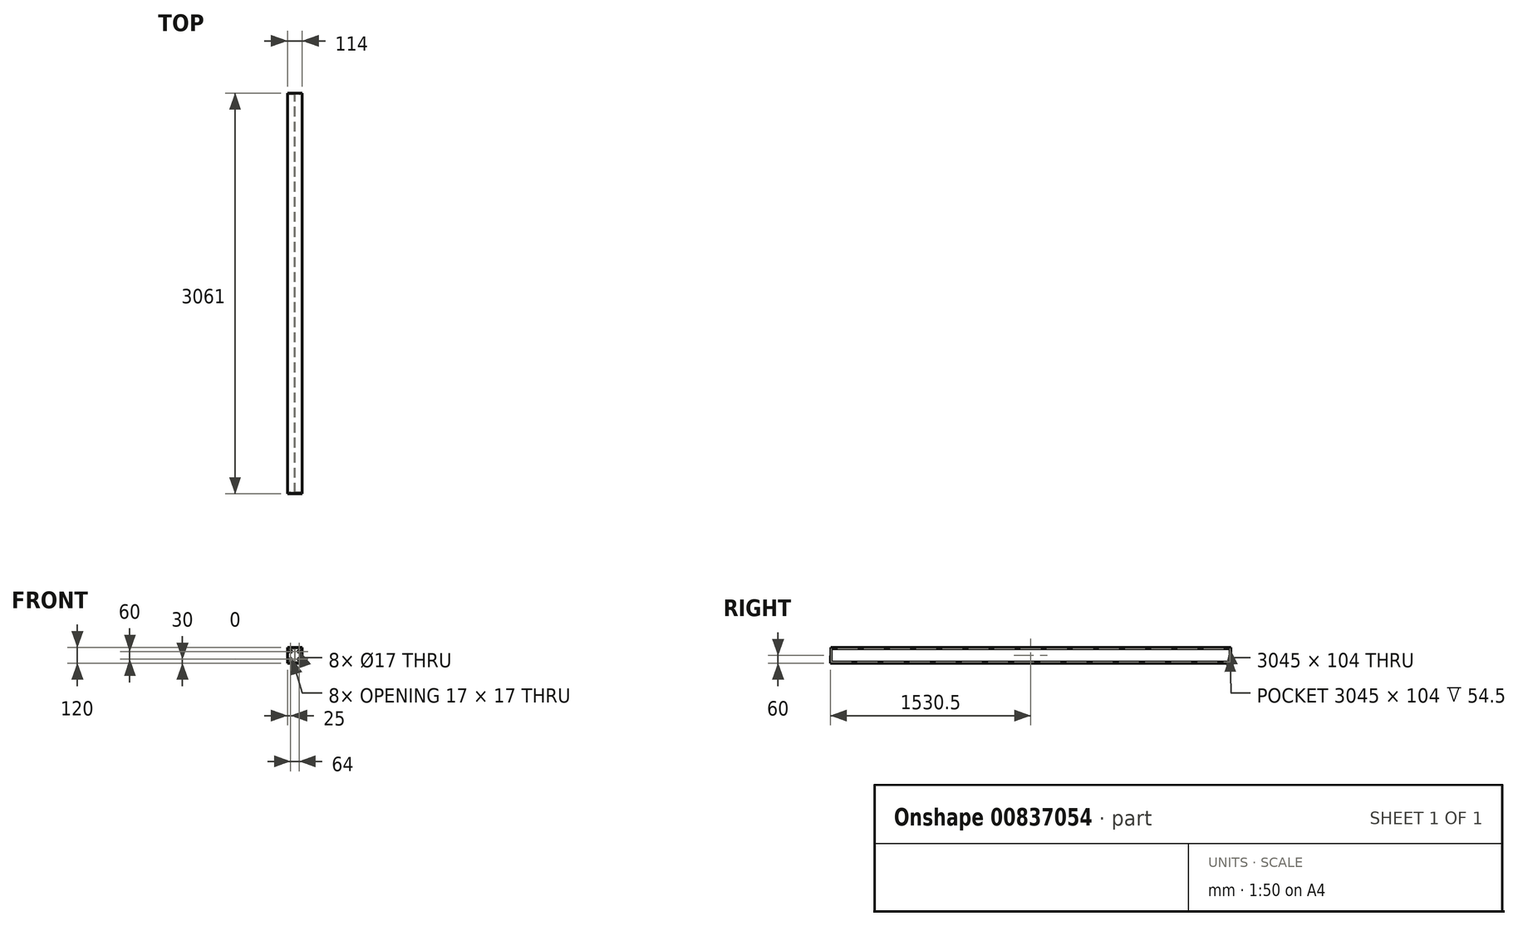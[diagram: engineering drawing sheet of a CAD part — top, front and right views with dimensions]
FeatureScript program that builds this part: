
annotation { "Feature Type Name" : "Feature", "Feature Type Description" : "" }
export const myFeature = defineFeature(function(context is Context, id is Id, definition is map)
    precondition{}
    {
        {
            var Q0;
            Q0=qCreatedBy(makeId("Front.planeOp"),FACE);
            var sketch = newSketch(context, id + "F0", { "sketchPlane" : qUnion([Q0])});
            skLineSegment(sketch, "E0", {"start": v(0, 60) * mm, "end": v(-57, 60) * mm});
            skLineSegment(sketch, "E1", {"start": v(-57, 60) * mm, "end": v(-57, 52) * mm});
            skLineSegment(sketch, "E2", {"start": v(-57, 52) * mm, "end": v(-2.5, 52) * mm});
            skLineSegment(sketch, "E3", {"start": v(-2.5, 52) * mm, "end": v(-2.5, 0) * mm});
            skLineSegment(sketch, "E4.MirrorCS", {"start": v(2.5, 52) * mm, "end": v(2.5, 0) * mm});
            skLineSegment(sketch, "E5.MirrorCS", {"start": v(57, 52) * mm, "end": v(2.5, 52) * mm});
            skLineSegment(sketch, "E6.MirrorCS", {"start": v(0, 60) * mm, "end": v(57, 60) * mm});
            skLineSegment(sketch, "E7.MirrorCS", {"start": v(57, 60) * mm, "end": v(57, 52) * mm});
            skLineSegment(sketch, "E8.MirrorCS", {"start": v(-2.5, -52) * mm, "end": v(-2.5, 0) * mm});
            skLineSegment(sketch, "E9.MirrorCS", {"start": v(-57, -52) * mm, "end": v(-2.5, -52) * mm});
            skLineSegment(sketch, "E10.MirrorCS", {"start": v(-57, -60) * mm, "end": v(-57, -52) * mm});
            skLineSegment(sketch, "E11.MirrorCS", {"start": v(0, -60) * mm, "end": v(-57, -60) * mm});
            skLineSegment(sketch, "E12.MirrorCS", {"start": v(0, -60) * mm, "end": v(57, -60) * mm});
            skLineSegment(sketch, "E13.MirrorCS", {"start": v(57, -60) * mm, "end": v(57, -52) * mm});
            skLineSegment(sketch, "E14.MirrorCS", {"start": v(57, -52) * mm, "end": v(2.5, -52) * mm});
            skLineSegment(sketch, "E15.MirrorCS", {"start": v(2.5, -52) * mm, "end": v(2.5, 0) * mm});
            skSolve(sketch);
        }
        {
            var Q0;
            Q0=qSketchRegion(id+"F0",true);
            extrude(context, id + "F1", {"entities" : qUnion([Q0]), "depth" : 3045 * mm, "offsetDistance" : 25 * mm});
        }
        {
            var Q0;
            Q0=makeQuery(id+"F1.opExtrude","CAP_FACE",FACE,{"disambiguationData":[OSD([sQuery(id+"F0.wireOp",EDGE,"E0"),sQuery(id+"F0.wireOp",EDGE,"E1"),sQuery(id+"F0.wireOp",EDGE,"E2"),sQuery(id+"F0.wireOp",EDGE,"E3"),sQuery(id+"F0.wireOp",EDGE,"E4.MirrorCS"),sQuery(id+"F0.wireOp",EDGE,"E5.MirrorCS"),sQuery(id+"F0.wireOp",EDGE,"E6.MirrorCS"),sQuery(id+"F0.wireOp",EDGE,"E7.MirrorCS"),sQuery(id+"F0.wireOp",EDGE,"E8.MirrorCS"),sQuery(id+"F0.wireOp",EDGE,"E9.MirrorCS"),sQuery(id+"F0.wireOp",EDGE,"E10.MirrorCS"),sQuery(id+"F0.wireOp",EDGE,"E11.MirrorCS"),sQuery(id+"F0.wireOp",EDGE,"E12.MirrorCS"),sQuery(id+"F0.wireOp",EDGE,"E13.MirrorCS"),sQuery(id+"F0.wireOp",EDGE,"E14.MirrorCS"),sQuery(id+"F0.wireOp",EDGE,"E15.MirrorCS")])],"isStart":false});
            var sketch = newSketch(context, id + "F2", { "sketchPlane" : qUnion([Q0])});
            skLineSegment(sketch, "E16.bottom", {"start": v(-57, 60) * mm, "end": v(57, 60) * mm});
            skLineSegment(sketch, "E16.top", {"start": v(-57, -60) * mm, "end": v(57, -60) * mm});
            skLineSegment(sketch, "E16.left", {"start": v(-57, 60) * mm, "end": v(-57, -60) * mm});
            skLineSegment(sketch, "E16.right", {"start": v(57, 60) * mm, "end": v(57, -60) * mm});
            skCircle(sketch, "E17", {"center": v(-32, 30) * mm, "radius": 8.5 * mm});
            skCircle(sketch, "E18.MirrorC", {"center": v(32, 30) * mm, "radius": 8.5 * mm});
            skCircle(sketch, "E19.MirrorC", {"center": v(-32, -30) * mm, "radius": 8.5 * mm});
            skCircle(sketch, "E20.MirrorC", {"center": v(32, -30) * mm, "radius": 8.5 * mm});
            skSolve(sketch);
        }
        {
            var Q0;
            Q0 = qSketchRegion(id + "F2", true);
            extrude(context, id + "F3", {"entities" : qUnion([Q0]), "operationType" : NewBodyOperationType.ADD, "depth" : 8 * mm, "offsetDistance" : 25 * mm});
        }
        {
            var Q0;
            Q0=makeQuery(id+"F1.opExtrude","CAP_FACE",FACE,{"disambiguationData":[OSD([sQuery(id+"F0.wireOp",EDGE,"E0"),sQuery(id+"F0.wireOp",EDGE,"E1"),sQuery(id+"F0.wireOp",EDGE,"E2"),sQuery(id+"F0.wireOp",EDGE,"E3"),sQuery(id+"F0.wireOp",EDGE,"E4.MirrorCS"),sQuery(id+"F0.wireOp",EDGE,"E5.MirrorCS"),sQuery(id+"F0.wireOp",EDGE,"E6.MirrorCS"),sQuery(id+"F0.wireOp",EDGE,"E7.MirrorCS"),sQuery(id+"F0.wireOp",EDGE,"E8.MirrorCS"),sQuery(id+"F0.wireOp",EDGE,"E9.MirrorCS"),sQuery(id+"F0.wireOp",EDGE,"E10.MirrorCS"),sQuery(id+"F0.wireOp",EDGE,"E11.MirrorCS"),sQuery(id+"F0.wireOp",EDGE,"E12.MirrorCS"),sQuery(id+"F0.wireOp",EDGE,"E13.MirrorCS"),sQuery(id+"F0.wireOp",EDGE,"E14.MirrorCS"),sQuery(id+"F0.wireOp",EDGE,"E15.MirrorCS")])],"isStart":true});
            var sketch = newSketch(context, id + "F4", { "sketchPlane" : qUnion([Q0])});
            skLineSegment(sketch, "E21.bottom", {"start": v(-57, 60) * mm, "end": v(57, 60) * mm});
            skLineSegment(sketch, "E21.top", {"start": v(-57, -60) * mm, "end": v(57, -60) * mm});
            skLineSegment(sketch, "E21.left", {"start": v(-57, 60) * mm, "end": v(-57, -60) * mm});
            skLineSegment(sketch, "E21.right", {"start": v(57, 60) * mm, "end": v(57, -60) * mm});
            skCircle(sketch, "E22", {"center": v(-32, 30) * mm, "radius": 8.5 * mm});
            skCircle(sketch, "E23.MirrorC", {"center": v(32, 30) * mm, "radius": 8.5 * mm});
            skCircle(sketch, "E24.MirrorC", {"center": v(-32, -30) * mm, "radius": 8.5 * mm});
            skCircle(sketch, "E25.MirrorC", {"center": v(32, -30) * mm, "radius": 8.5 * mm});
            skSolve(sketch);
        }
        {
            var Q0;
            Q0 = qSketchRegion(id + "F4", true);
            extrude(context, id + "F5", {"entities" : qUnion([Q0]), "operationType" : NewBodyOperationType.ADD, "depth" : 8 * mm, "offsetDistance" : 25 * mm});
        }
        {
            var Q0;
            Q0=qCreatedBy(makeId("Right.planeOp"),FACE);
            var sketch = newSketch(context, id + "F6", { "sketchPlane" : qUnion([Q0])});
            skLineSegment(sketch, "E26", {"start": v(32.16, 60) * mm, "end": v(8, 60) * mm});
            skLineSegment(sketch, "E27", {"start": v(8, 60) * mm, "end": v(4.86, -60) * mm});
            skLineSegment(sketch, "E28", {"start": v(4.86, -60) * mm, "end": v(32.16, -60) * mm});
            skLineSegment(sketch, "E29", {"start": v(32.16, -60) * mm, "end": v(32.16, 60) * mm});
            skLineSegment(sketch, "E30", {"start": v(-3049.86, 60) * mm, "end": v(-3053, -60) * mm});
            skLineSegment(sketch, "E31", {"start": v(-3053, -60) * mm, "end": v(-3064.5, -60) * mm});
            skLineSegment(sketch, "E32", {"start": v(-3064.5, -60) * mm, "end": v(-3064.5, 60) * mm});
            skLineSegment(sketch, "E33", {"start": v(-3064.5, 60) * mm, "end": v(-3049.86, 60) * mm});
            skSolve(sketch);
        }
        {
            var Q0;
            Q0 = qSketchRegion(id + "F6", true);
            extrude(context, id + "F7", {"entities" : qUnion([Q0]), "operationType" : NewBodyOperationType.REMOVE, "oppositeDirection" : true, "depth" : 150 * mm, "offsetDistance" : 25 * mm, "symmetric" : true});
        }
    });
